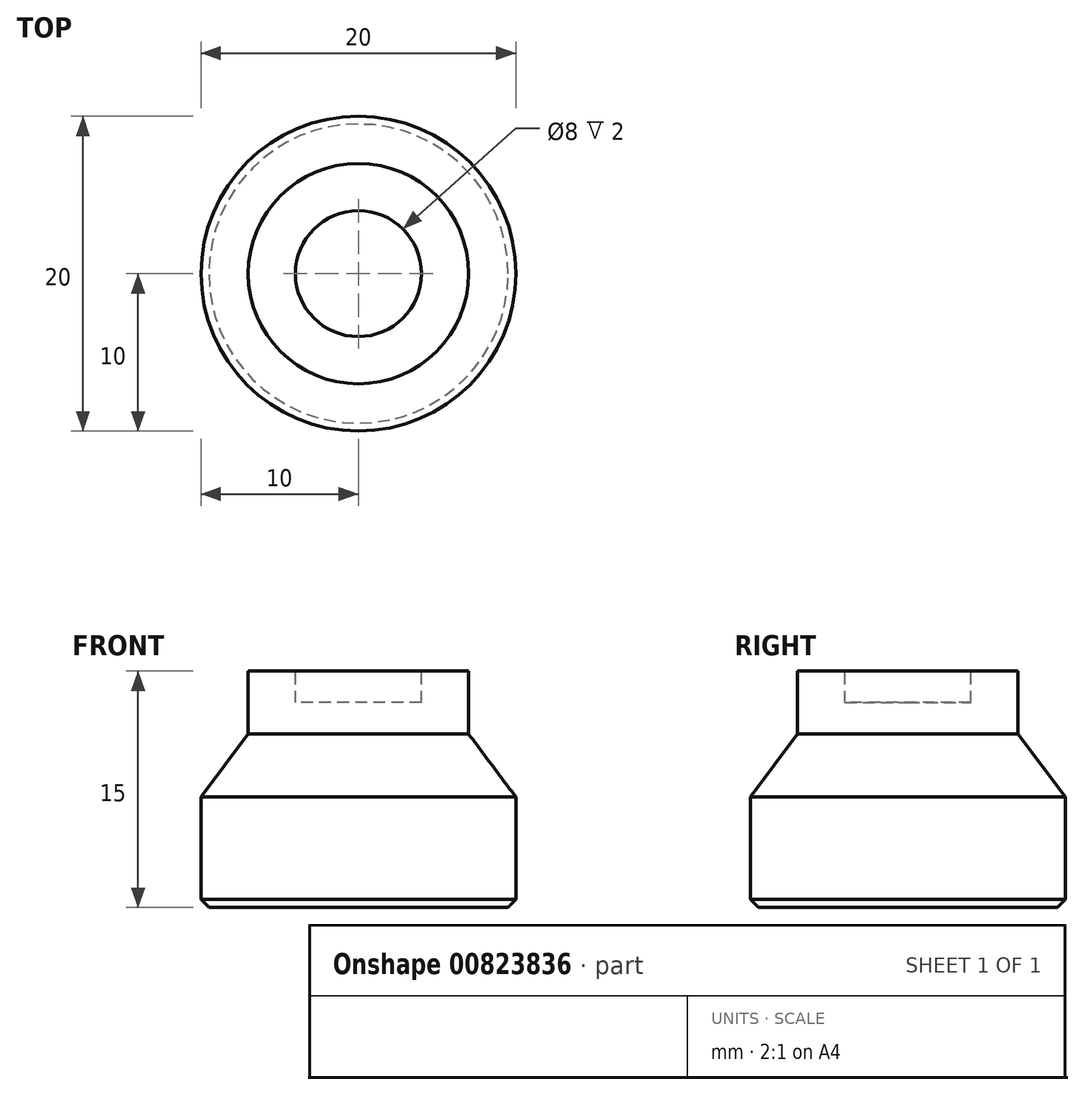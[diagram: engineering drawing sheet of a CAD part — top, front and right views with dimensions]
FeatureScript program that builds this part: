
annotation { "Feature Type Name" : "Feature", "Feature Type Description" : "" }
export const myFeature = defineFeature(function(context is Context, id is Id, definition is map)
    precondition{}
    {
        {
            var Q0;
            Q0=qCreatedBy(makeId("Front.planeOp"),FACE);
            var sketch = newSketch(context, id + "F0", { "sketchPlane" : qUnion([Q0])});
            skLineSegment(sketch, "E0", {"start": v(0, 0) * mm, "end": v(10, 0) * mm});
            skLineSegment(sketch, "E1", {"start": v(10, 0) * mm, "end": v(10, 7) * mm});
            skLineSegment(sketch, "E2", {"start": v(10, 7) * mm, "end": v(7, 11) * mm});
            skLineSegment(sketch, "E3", {"start": v(7, 11) * mm, "end": v(7, 15) * mm});
            skLineSegment(sketch, "E4", {"start": v(7, 15) * mm, "end": v(0, 15) * mm});
            skLineSegment(sketch, "E5", {"start": v(0, 15) * mm, "end": v(0, 0) * mm});
            skSolve(sketch);
        }
        {
            var Q0;
            Q0=makeQuery(id+"F0.imprint","IMPRINT",FACE,{"disambiguationData":[TD([[makeQuery(id+"F0.imprint","IMPRINT",EDGE,{"derivedFrom":sQuery(id+"F0.wireOp",EDGE,"E0")}),1.0]])]});
            var Q1;
            Q1=sQuery(id+"F0.wireOp",EDGE,"E5");
            revolve(context, id + "F1", {"surfaceOperationType" : NewSurfaceOperationType.NEW, "entities" : qUnion([Q0]), "axis" : qUnion([Q1]), "revolveType" : RevolveType.FULL});
        }
        {
            var Q0;
            Q0=makeQuery(id+"F1.opRevolve","SWEPT_FACE",FACE,{"disambiguationData":[OSD([sQuery(id+"F0.wireOp",EDGE,"E4")])]});
            var sketch = newSketch(context, id + "F2", { "sketchPlane" : qUnion([Q0])});
            skCircle(sketch, "E6", {"center": v(0, 0) * mm, "radius": 4 * mm});
            skSolve(sketch);
        }
        {
            var Q0;
            Q0=makeQuery(id+"F2.imprint","IMPRINT",FACE,{"disambiguationData":[TD([[makeQuery(id+"F2.imprint","IMPRINT",EDGE,{"derivedFrom":sQuery(id+"F2.wireOp",EDGE,"E6")}),1.0]])]});
            var Q1;
            Q1=sQuery(id+"F2.wireOp",EDGE,"E6");
            extrude(context, id + "F3", {"entities" : qUnion([Q0]), "operationType" : NewBodyOperationType.REMOVE, "surfaceEntities" : qUnion([Q1]), "oppositeDirection" : true, "depth" : 2 * mm, "offsetDistance" : 25 * mm});
        }
        {
            var Q0;
            Q0=makeQuery(id+"F1.opRevolve","SWEPT_EDGE",EDGE,{"disambiguationData":[OSD([sQuery(id+"F0.wireOp",EDGE,"E0"),sQuery(id+"F0.wireOp",EDGE,"E1")])]});
            chamfer(context, id + "F4", {"entities" : qUnion([Q0]), "width" : .5 * mm, "tangentPropagation" : true});
        }
    });
